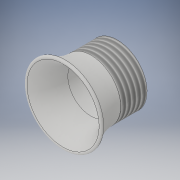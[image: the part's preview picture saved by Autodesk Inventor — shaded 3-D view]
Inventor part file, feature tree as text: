
AUTODESK INVENTOR PART (.ipt)
format: ipt  version: 2018 (Build 220112000, 112)  size: 171,520 bytes
history: native  units: mm
features: revolve x1, thread x1, sketch x1
ambient origin geometry x8: Origin, YZ Plane, XZ Plane, XY Plane, X Axis, Y Axis, Z Axis, Center Point
bodies: Solid1 (feature_tree)
feature tree (3):
  revolve  "Revolution1"  [1 undecoded]
  thread  "Thread1"  [1 undecoded]
  sketch  "Sketch1"  dims[d0=8.28mm d1=5.87mm d2=3.5mm d4=4.5mm d5=4.0mm d6=0.5mm d7=6.362336mm d8=90.0deg d9=10.0mm d10=0.0mm]
note: 2 required parameter values undecoded (feature->parameter linkage not recoverable at this tier; creation-order binding heuristic only, values carry confidence <= 0.55)